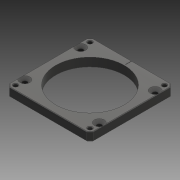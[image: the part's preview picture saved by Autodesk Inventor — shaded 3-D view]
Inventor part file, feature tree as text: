
AUTODESK INVENTOR PART (.ipt)
format: ipt  version: 2023 (Build 270158000, 158)  size: 189,440 bytes
history: native  units: mm
features: other x1, extrude x1, sketch x1, imported_body x1
ambient origin geometry x8: Origin, YZ Plane, XZ Plane, XY Plane, X Axis, Y Axis, Z Axis, Center Point
bodies: Body1 (feature_tree)
feature tree (4):
  other  "ソリッド1"
  extrude  "押し出し1"  TaperAngle=0.0deg  [1 undecoded]
  sketch  "スケッチ1"
  imported_body  "Base1"
note: 1 required parameter value undecoded (feature->parameter linkage not recoverable at this tier; creation-order binding heuristic only, values carry confidence <= 0.55)
